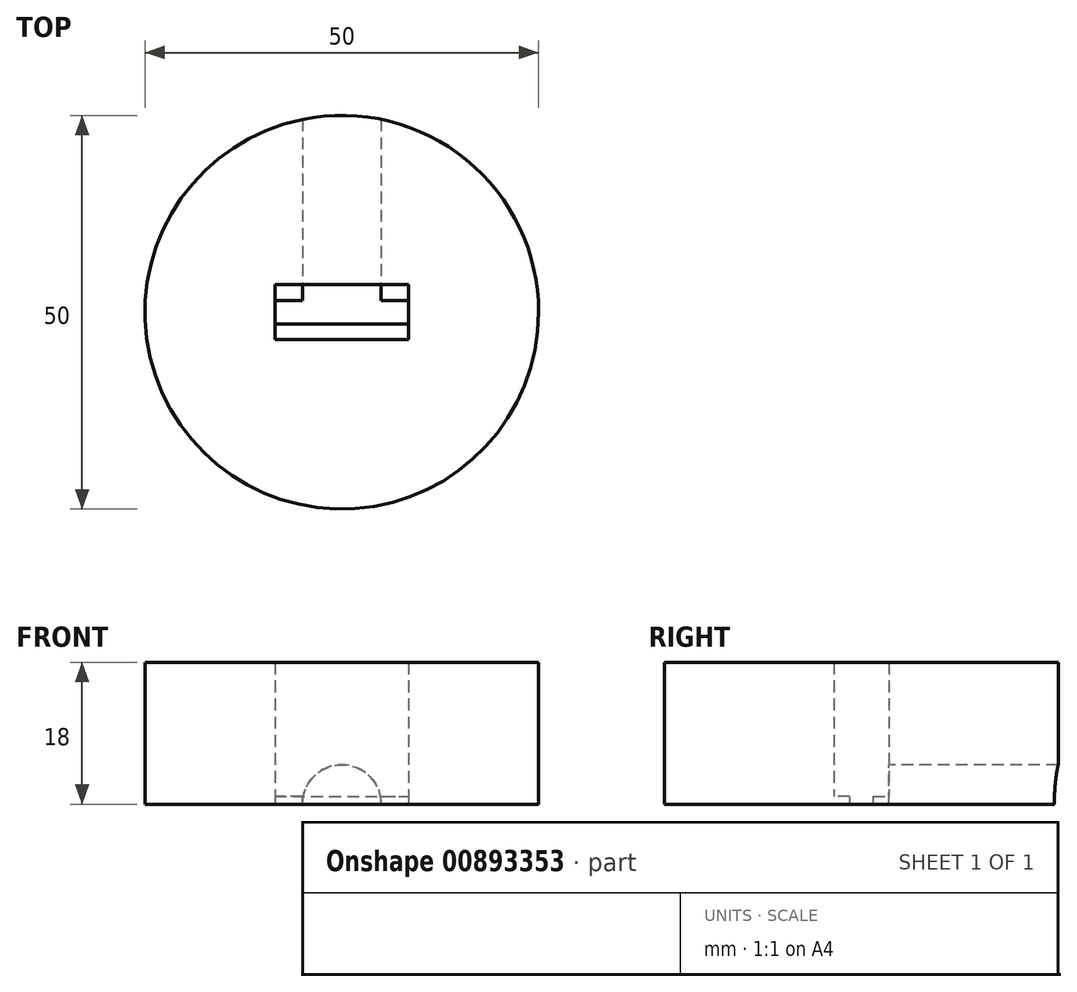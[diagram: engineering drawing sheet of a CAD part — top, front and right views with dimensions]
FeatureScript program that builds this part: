
annotation { "Feature Type Name" : "Feature", "Feature Type Description" : "" }
export const myFeature = defineFeature(function(context is Context, id is Id, definition is map)
    precondition{}
    {
        {
            var Q0;
            Q0=qCreatedBy(makeId("Top.planeOp"),FACE);
            var sketch = newSketch(context, id + "F0", { "sketchPlane" : qUnion([Q0])});
            skCircle(sketch, "E0", {"center": v(0, 0) * mm, "radius": 25 * mm});
            skLineSegment(sketch, "E1.bottom", {"start": v(-8.5, 3.5) * mm, "end": v(8.5, 3.5) * mm});
            skLineSegment(sketch, "E1.top", {"start": v(-8.5, -3.5) * mm, "end": v(8.5, -3.5) * mm});
            skLineSegment(sketch, "E1.left", {"start": v(-8.5, 3.5) * mm, "end": v(-8.5, -3.5) * mm});
            skLineSegment(sketch, "E1.right", {"start": v(8.5, 3.5) * mm, "end": v(8.5, -3.5) * mm});
            skSolve(sketch);
        }
        {
            var Q0;
            Q0=makeQuery(id+"F0.imprint","IMPRINT",FACE,{"disambiguationData":[TD([[makeQuery(id+"F0.imprint","IMPRINT",EDGE,{"derivedFrom":sQuery(id+"F0.wireOp",EDGE,"E0")}),1.0]])]});
            extrude(context, id + "F1", {"entities" : qUnion([Q0]), "depth" : 18 * mm, "offsetDistance" : 25 * mm});
        }
        {
            var Q0;
            Q0=makeQuery(id+"F1.opExtrude","SWEPT_FACE",FACE,{"disambiguationData":[OSD([sQuery(id+"F0.wireOp",EDGE,"E1.top")])]});
            var sketch = newSketch(context, id + "F2", { "sketchPlane" : qUnion([Q0])});
            skLineSegment(sketch, "E2", {"start": v(8.5, 0) * mm, "end": v(-8.5, 9) * mm});
            skLineSegment(sketch, "E3", {"start": v(-8.5, 9) * mm, "end": v(-8.5, 0) * mm});
            skLineSegment(sketch, "E4", {"start": v(-8.5, 0) * mm, "end": v(8.5, 0) * mm});
            skLineSegment(sketch, "E5", {"start": v(8.5, 9) * mm, "end": v(-8.5, 9) * mm});
            skLineSegment(sketch, "E6", {"start": v(8.5, 9) * mm, "end": v(8.5, 0) * mm});
            skLineSegment(sketch, "E7", {"start": v(0, 4.5) * mm, "end": v(0, 0) * mm});
            skCircle(sketch, "E8", {"center": v(0, 0) * mm, "radius": 4.5 * mm});
            skPoint(sketch, "E9", {"position": v(4.5, 0) * mm});
            skPoint(sketch, "E10", {"position": v(-4.5, 0) * mm});
            skSolve(sketch);
        }
        {
            var Q0;
            Q0=sQuery(id+"F2.wireOp",VERTEX,"E7.end");
            var Q1;
            Q1=makeQuery(id+"F1.opExtrude","SWEPT_BODY",BODY,{"disambiguationData":[OSD([sQuery(id+"F0.wireOp",EDGE,"E0"),sQuery(id+"F0.wireOp",EDGE,"E1.bottom"),sQuery(id+"F0.wireOp",EDGE,"E1.top"),sQuery(id+"F0.wireOp",EDGE,"E1.left"),sQuery(id+"F0.wireOp",EDGE,"E1.right")])]});
            hole(context, id + "F3", {"style" : HoleStyle.SIMPLE, "endStyle" : HoleEndStyle.BLIND, "oppositeDirection" : true, "holeDiameter" : 10 * mm, "majorDiameter" : 5 * mm, "holeDepth" : 100 * mm, "isTappedThrough" : true, "tappedDepth" : 12 * mm, "tapClearance" : 3, "locations" : qUnion([Q0]), "scope" : qUnion([Q1])});
        }
        {
            var Q0;
            Q0=makeQuery(id+"F1.opExtrude","SWEPT_FACE",FACE,{"disambiguationData":[OSD([sQuery(id+"F0.wireOp",EDGE,"E1.top")])]});
            var sketch = newSketch(context, id + "F4", { "sketchPlane" : qUnion([Q0])});
            skLineSegment(sketch, "E11.bottom", {"start": v(8.5, 0) * mm, "end": v(-8.5, 0) * mm});
            skLineSegment(sketch, "E11.top", {"start": v(8.5, 1) * mm, "end": v(-8.5, 1) * mm});
            skLineSegment(sketch, "E11.left", {"start": v(8.5, 0) * mm, "end": v(8.5, 1) * mm});
            skLineSegment(sketch, "E11.right", {"start": v(-8.5, 0) * mm, "end": v(-8.5, 1) * mm});
            skSolve(sketch);
        }
        {
            var Q0;
            Q0 = qSketchRegion(id + "F4", true);
            extrude(context, id + "F5", {"entities" : qUnion([Q0]), "operationType" : NewBodyOperationType.ADD, "depth" : 2 * mm, "offsetDistance" : 25 * mm});
        }
        {
            var Q0;
            Q0=makeQuery(id+"F1.opExtrude","SWEPT_FACE",FACE,{"disambiguationData":[OSD([sQuery(id+"F0.wireOp",EDGE,"E1.bottom")])]});
            var sketch = newSketch(context, id + "F6", { "sketchPlane" : qUnion([Q0])});
            skLineSegment(sketch, "E12.bottom", {"start": v(-5, 0) * mm, "end": v(-8.5, 0) * mm});
            skLineSegment(sketch, "E12.top", {"start": v(-5, 1) * mm, "end": v(-8.5, 1) * mm});
            skLineSegment(sketch, "E12.left", {"start": v(-5, 0) * mm, "end": v(-5, 1) * mm});
            skLineSegment(sketch, "E12.right", {"start": v(-8.5, 0) * mm, "end": v(-8.5, 1) * mm});
            skLineSegment(sketch, "E13.bottom", {"start": v(5, 0) * mm, "end": v(8.5, 0) * mm});
            skLineSegment(sketch, "E13.top", {"start": v(5, 1) * mm, "end": v(8.5, 1) * mm});
            skLineSegment(sketch, "E13.left", {"start": v(5, 0) * mm, "end": v(5, 1) * mm});
            skLineSegment(sketch, "E13.right", {"start": v(8.5, 0) * mm, "end": v(8.5, 1) * mm});
            skSolve(sketch);
        }
        {
            var Q0;
            Q0=makeQuery(id+"F6.imprint","IMPRINT",FACE,{"disambiguationData":[TD([[makeQuery(id+"F6.imprint","IMPRINT",EDGE,{"derivedFrom":sQuery(id+"F6.wireOp",EDGE,"E12.bottom")}),1.0]])]});
            var Q1;
            Q1=makeQuery(id+"F6.imprint","IMPRINT",FACE,{"disambiguationData":[TD([[makeQuery(id+"F6.imprint","IMPRINT",EDGE,{"derivedFrom":sQuery(id+"F6.wireOp",EDGE,"E13.bottom")}),1.0]])]});
            extrude(context, id + "F7", {"entities" : qUnion([Q0, Q1]), "operationType" : NewBodyOperationType.ADD, "depth" : 2 * mm, "offsetDistance" : 25 * mm});
        }
    });
